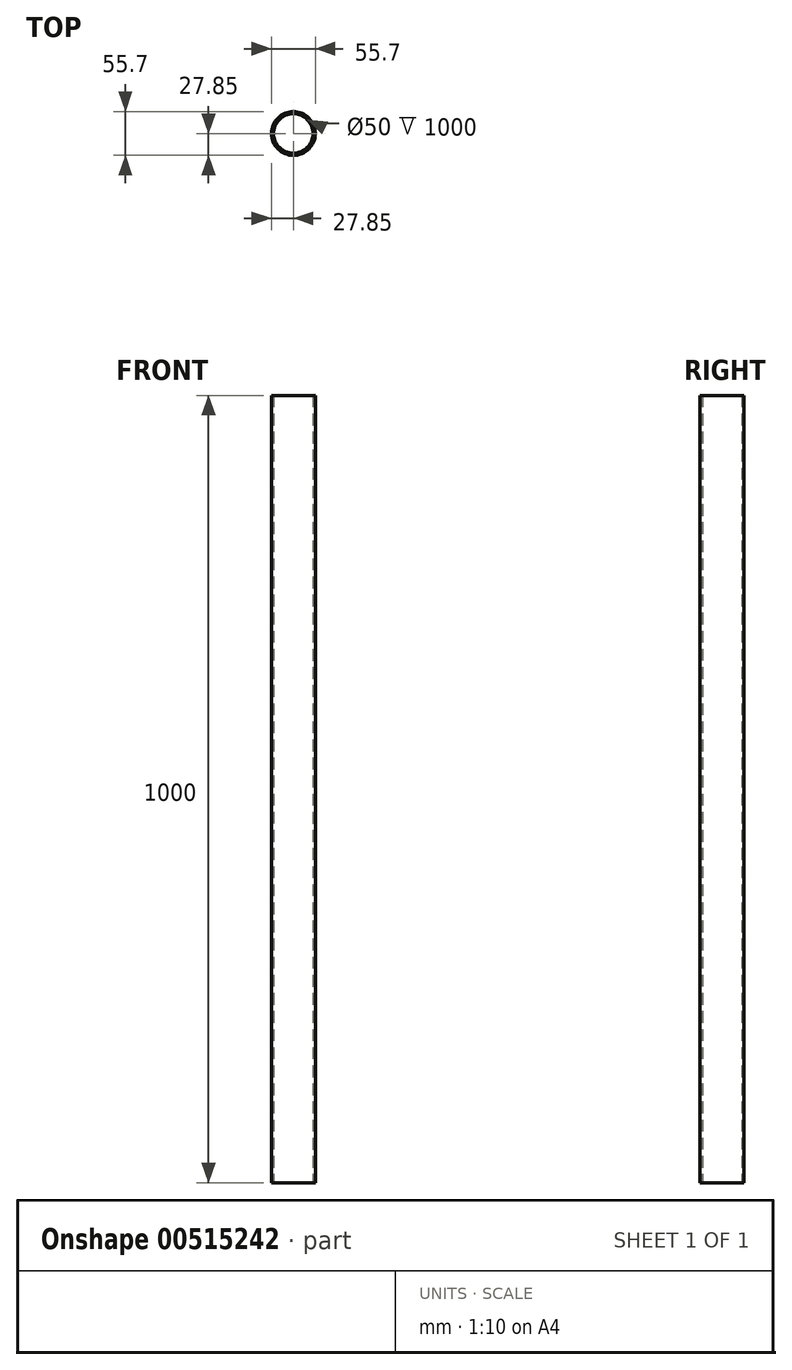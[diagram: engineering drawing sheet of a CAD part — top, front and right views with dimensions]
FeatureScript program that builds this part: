
annotation { "Feature Type Name" : "Feature", "Feature Type Description" : "" }
export const myFeature = defineFeature(function(context is Context, id is Id, definition is map)
    precondition{}
    {
        {
            var Q0;
            Q0=qCreatedBy(makeId("Top.planeOp"),FACE);
            var sketch = newSketch(context, id + "F0", { "sketchPlane" : qUnion([Q0])});
            skCircle(sketch, "E0", {"center": v(0, 0) * mm, "radius": 27.85 * mm});
            skCircle(sketch, "E1", {"center": v(0, 0) * mm, "radius": 25 * mm});
            skSolve(sketch);
        }
        {
            var Q0;
            Q0=makeQuery(id+"F0.imprint","IMPRINT",FACE,{"disambiguationData":[TD([[makeQuery(id+"F0.imprint","IMPRINT",EDGE,{"derivedFrom":sQuery(id+"F0.wireOp",EDGE,"E0")}),1.0]])]});
            extrude(context, id + "F1", {"entities" : qUnion([Q0]), "depth" : 1000 * mm, "offsetDistance" : 25 * mm});
        }
    });
